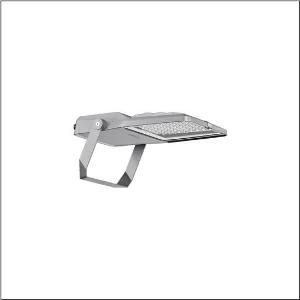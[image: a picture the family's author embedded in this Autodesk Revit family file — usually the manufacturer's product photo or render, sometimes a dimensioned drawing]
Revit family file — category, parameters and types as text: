
# Revit family: floodlight_fl_21_iq_mini___pl43_5xa7772d2a1a_725a
name_source: partatom
category: Lighting Fixtures
units: mm (PartAtom-declared; Revit-internal decimal feet)

## family parameters
Cut with Voids When Loaded = No
Host = Face
Light Source = No
Part Type = Normal
Room Calculation Point = No
Round Connector Dimension = Use Diameter
Shared = No

## types (1)
- --- (1 x LED, 18290 lm, 143 W, 3000K)
    Apparent Load = 143 VA
    CIE Flux Codes = 27 78 99 100 100
    Color Rendering = 70
    Color Temperature = 3000K
    Default Elevation = 1800 mm
    Description = Floodlight FL 21 iQ mini, floodlight, primary light control with lens, of PMMA, primary optical cover: protective disc, of toughened safety glass, transparent, light distribution: PL43, light emission: direct distribution, installation type: surface-mounted, LED, High Power LED, rated luminous flux: 18.290lm, luminous efficacy: 128lm/W, light colour: 730, colour temperature: 3000K, control: Street-Remote, Auto-Match, Temp-Guard, Night-Set, Smart-Wire, Desk-Remote (wireless, voltage-free reading and setting of iQ features in the workshop via application-optimized NFC function/RFID function), optimised constant luminous flux control (CLO 2.0), with terminal, 6-pole, mains connection: 220..240V, AC, 50/60Hz, start of lifetime: 143W, end of service life: 152W, reduction: 61W, luminaire housing, of diecast aluminium, powder-coated, Siteco® metallic grey (DB 702S), corrosivity category C5 mid according to DIN EN ISO 12944, sealing non-destructively replaceable, mounting bracket, of steel, galvanised, powder-coated, Siteco® metallic grey (DB 702S), protection rating (complete): IP66, insulation class (complete): insulation class II (safety insulation), certification: CE, ENEC, VDE, protection symbol: D, impact resistance: IK08, permissible operating ambient temperature: -40..+40°C, permissible operating ambient temperature for outdoor applications: -40..+50°C, standard: DIN EN 12944, LABS conformity tested according to VDMA 24364:2018-05, packaging unit: 1 piece

Light Distribution: PL43
    Height = 70 mm
    Lamp = 1 x LED
    Lamp Light Flux = 18290 lm
    Lamp Power = 143 W
    Lamp count = 1
    Length = 485 mm
    Luminous efficacy = 128 lm/W
    Manufacturer = Siteco
    ModVariant = No
    Model = 5XA7772D2A1A
    Number of Poles = 1
    OnlyDefault = Yes
    Power Factor = 1
    Product Name = Floodlight FL 21 iQ mini | PL43
    Product group = floodlight | pylon annexe
    ProductGroupID = 6200
    Protection Class = Protection class II
    Protection Degree = IP 66
    RLX_Detail_Level = 1
    RLX_Emergency_Light_Flux = 0 lm
    RLX_Emergency_Type = 0
    RLX_Emergency_Type_DB = No
    RlxData = <blob elided: 96329 chars, md5=bac4eb08>
    Socket = socket
    Standby Power = 0 W
    System Light Flux = 18290 lm
    System Power = 143 W
    Type Comments = factory setting: luminous flux: 100 % | dim-lin: 254 | 730 mA
    Type Image = l_1006845.jpg
    URL = http://relux.com
    VarID = @adj_094349
    Voltage = 0 V
    Weight = 0.00 kg
    Width = 337 mm

## geometry (parser evidence)
native form markers: Blend x4, Sweep x13
no freeform markers — native parametric forms only
